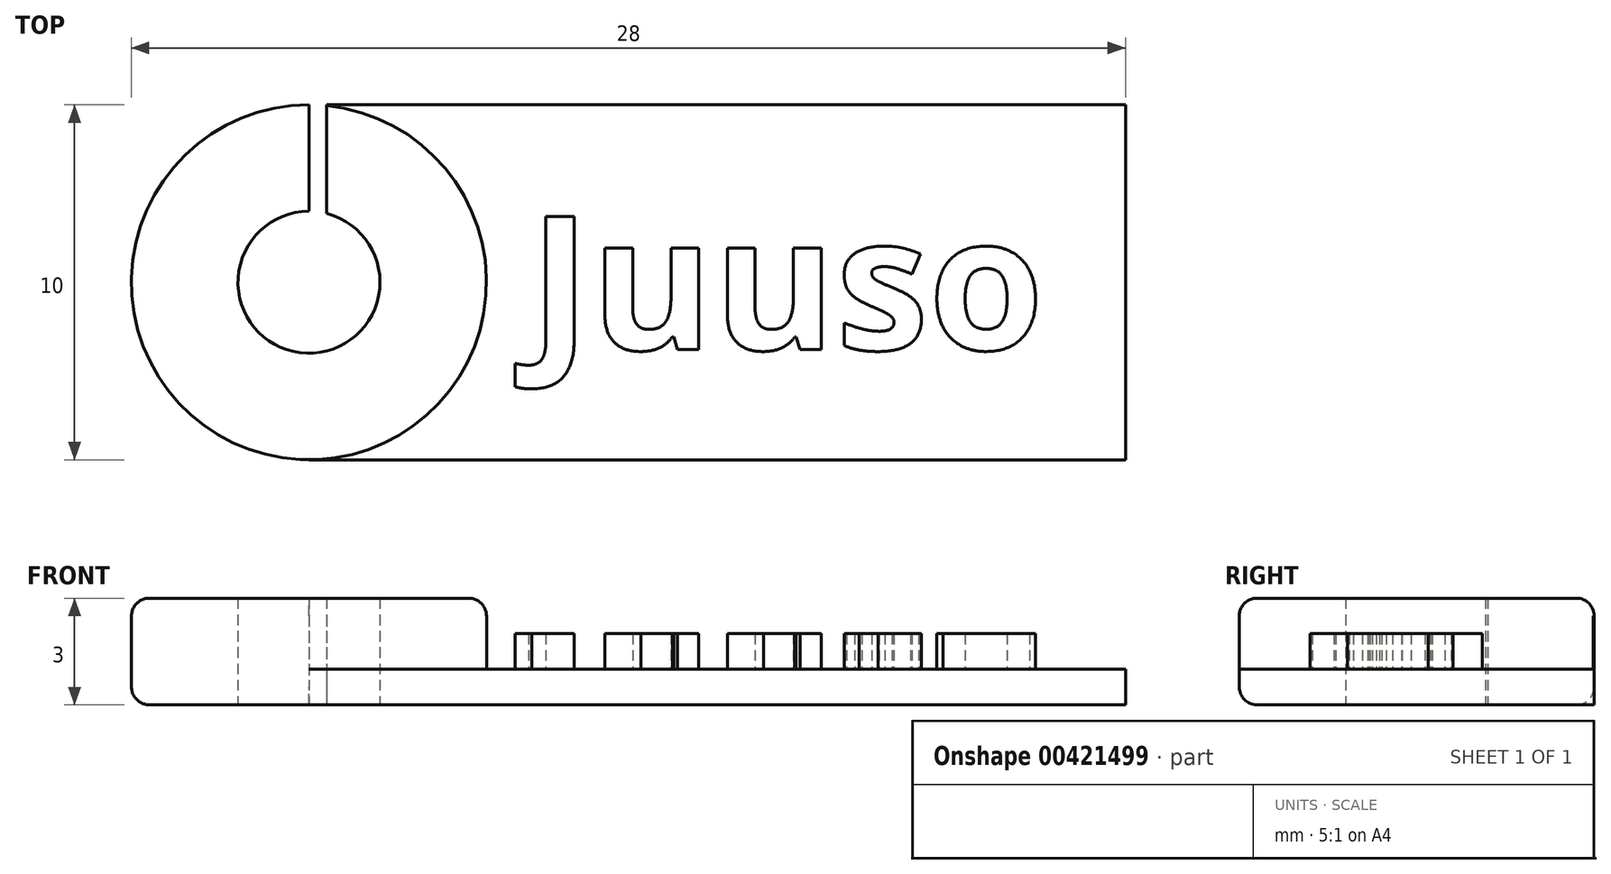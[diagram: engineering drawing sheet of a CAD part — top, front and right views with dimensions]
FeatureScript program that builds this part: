
annotation { "Feature Type Name" : "Feature", "Feature Type Description" : "" }
export const myFeature = defineFeature(function(context is Context, id is Id, definition is map)
    precondition{}
    {
        {
            var Q0;
            Q0=qCreatedBy(makeId("Top.planeOp"),FACE);
            var sketch = newSketch(context, id + "F0", { "sketchPlane" : qUnion([Q0])});
            skCircle(sketch, "E0", {"center": v(0, 0) * mm, "radius": 5 * mm});
            skCircle(sketch, "E1", {"center": v(0, 0) * mm, "radius": 2 * mm});
            skLineSegment(sketch, "E2", {"start": v(0, 5) * mm, "end": v(23, 5) * mm});
            skLineSegment(sketch, "E3", {"start": v(0, -5) * mm, "end": v(23, -5) * mm});
            skLineSegment(sketch, "E4", {"start": v(23, -5) * mm, "end": v(23, 5) * mm});
            skText(sketch, "E5", { "text": "Juuso", "fontName": "OpenSans-Bold.ttf"});
            skLineSegment(sketch, "E6", {"start": v(0, 5) * mm, "end": v(0, 2) * mm});
            skLineSegment(sketch, "E7", {"start": v(0.5, 5) * mm, "end": v(0.5, 1.94) * mm});
            const initialGuessF0  = {"E5": [0.0062, -0.0019, 1, 0, 0.00378]};
            skSetInitialGuess(sketch, initialGuessF0);
            skSolve(sketch);
        }
        {
            var Q0;
            {var subQ0=sQuery(id+"F0.wireOp",EDGE,"E6");Q0=makeQuery(id+"F0.imprint","IMPRINT",FACE,{"disambiguationData":[TD([[makeQuery(id+"F0.imprint","IMPRINT",EDGE,{"derivedFrom":subQ0}),-1.0]])]});}
            extrude(context, id + "F1", {"entities" : qUnion([Q0]), "depth" : 3 * mm, "offsetDistance" : 25 * mm});
        }
        {
            var Q0;
            {var subQ0=sQuery(id+"F0.wireOp",EDGE,"E3");Q0=makeQuery(id+"F0.imprint","IMPRINT",FACE,{"disambiguationData":[TD([[makeQuery(id+"F0.imprint","IMPRINT",EDGE,{"derivedFrom":subQ0}),1.0]])]});}
            var Q1;
            Q1=makeQuery(id+"F0.imprint","IMPRINT",FACE,{"disambiguationData":[TD([[makeQuery(id+"F0.imprint","IMPRINT",EDGE,{"derivedFrom":sQuery(id+"F0.wireOp",EDGE,"E5.sketch_text.stroke-78")}),1.0]])]});
            var Q2;
            Q2=makeQuery(id+"F0.imprint","IMPRINT",FACE,{"disambiguationData":[TD([[makeQuery(id+"F0.imprint","IMPRINT",EDGE,{"derivedFrom":sQuery(id+"F0.wireOp",EDGE,"E5.sketch_text.stroke-70")}),1.0]])]});
            extrude(context, id + "F2", {"entities" : qUnion([Q0, Q1, Q2]), "operationType" : NewBodyOperationType.ADD, "depth" : 1 * mm, "offsetDistance" : 25 * mm});
        }
        {
            var Q0;
            Q0=makeQuery(id+"F0.imprint","IMPRINT",FACE,{"disambiguationData":[TD([[makeQuery(id+"F0.imprint","IMPRINT",EDGE,{"derivedFrom":sQuery(id+"F0.wireOp",EDGE,"E5.sketch_text.stroke-0")}),-1.0]])]});
            var Q1;
            Q1=makeQuery(id+"F0.imprint","IMPRINT",FACE,{"disambiguationData":[TD([[makeQuery(id+"F0.imprint","IMPRINT",EDGE,{"derivedFrom":sQuery(id+"F0.wireOp",EDGE,"E5.sketch_text.stroke-10")}),-1.0]])]});
            var Q2;
            Q2=makeQuery(id+"F0.imprint","IMPRINT",FACE,{"disambiguationData":[TD([[makeQuery(id+"F0.imprint","IMPRINT",EDGE,{"derivedFrom":sQuery(id+"F0.wireOp",EDGE,"E5.sketch_text.stroke-27")}),-1.0]])]});
            var Q3;
            Q3=makeQuery(id+"F0.imprint","IMPRINT",FACE,{"disambiguationData":[TD([[makeQuery(id+"F0.imprint","IMPRINT",EDGE,{"derivedFrom":sQuery(id+"F0.wireOp",EDGE,"E5.sketch_text.stroke-44")}),-1.0]])]});
            var Q4;
            Q4=makeQuery(id+"F0.imprint","IMPRINT",FACE,{"disambiguationData":[TD([[makeQuery(id+"F0.imprint","IMPRINT",EDGE,{"derivedFrom":sQuery(id+"F0.wireOp",EDGE,"E5.sketch_text.stroke-69")}),-1.0]])]});
            var Q5;
            Q5=makeQuery(id+"F0.imprint","IMPRINT",FACE,{"disambiguationData":[TD([[makeQuery(id+"F0.imprint","IMPRINT",EDGE,{"derivedFrom":sQuery(id+"F0.wireOp",EDGE,"E5.sketch_text.stroke-70")}),-1.0]])]});
            extrude(context, id + "F3", {"entities" : qUnion([Q0, Q1, Q2, Q3, Q4, Q5]), "operationType" : NewBodyOperationType.ADD, "depth" : 2 * mm, "offsetDistance" : 25 * mm});
        }
        {
            var Q0;
            Q0=makeQuery(id+"F1.opExtrude","CAP_EDGE",EDGE,{"disambiguationData":[OSD([sQuery(id+"F0.wireOp",EDGE,"E0")])],"isStart":false});
            var Q1;
            Q1=makeQuery(id+"F1.opExtrude","CAP_EDGE",EDGE,{"disambiguationData":[OSD([sQuery(id+"F0.wireOp",EDGE,"E0")])],"isStart":true});
            fillet(context, id + "F4", {"entities" : qUnion([Q0, Q1]), "tangentPropagation" : true, "radius" : 0.5 * mm, "defaultsChanged" : true, "vertexSettings" : [], "allowEdgeOverflow" : false});
        }
    });
